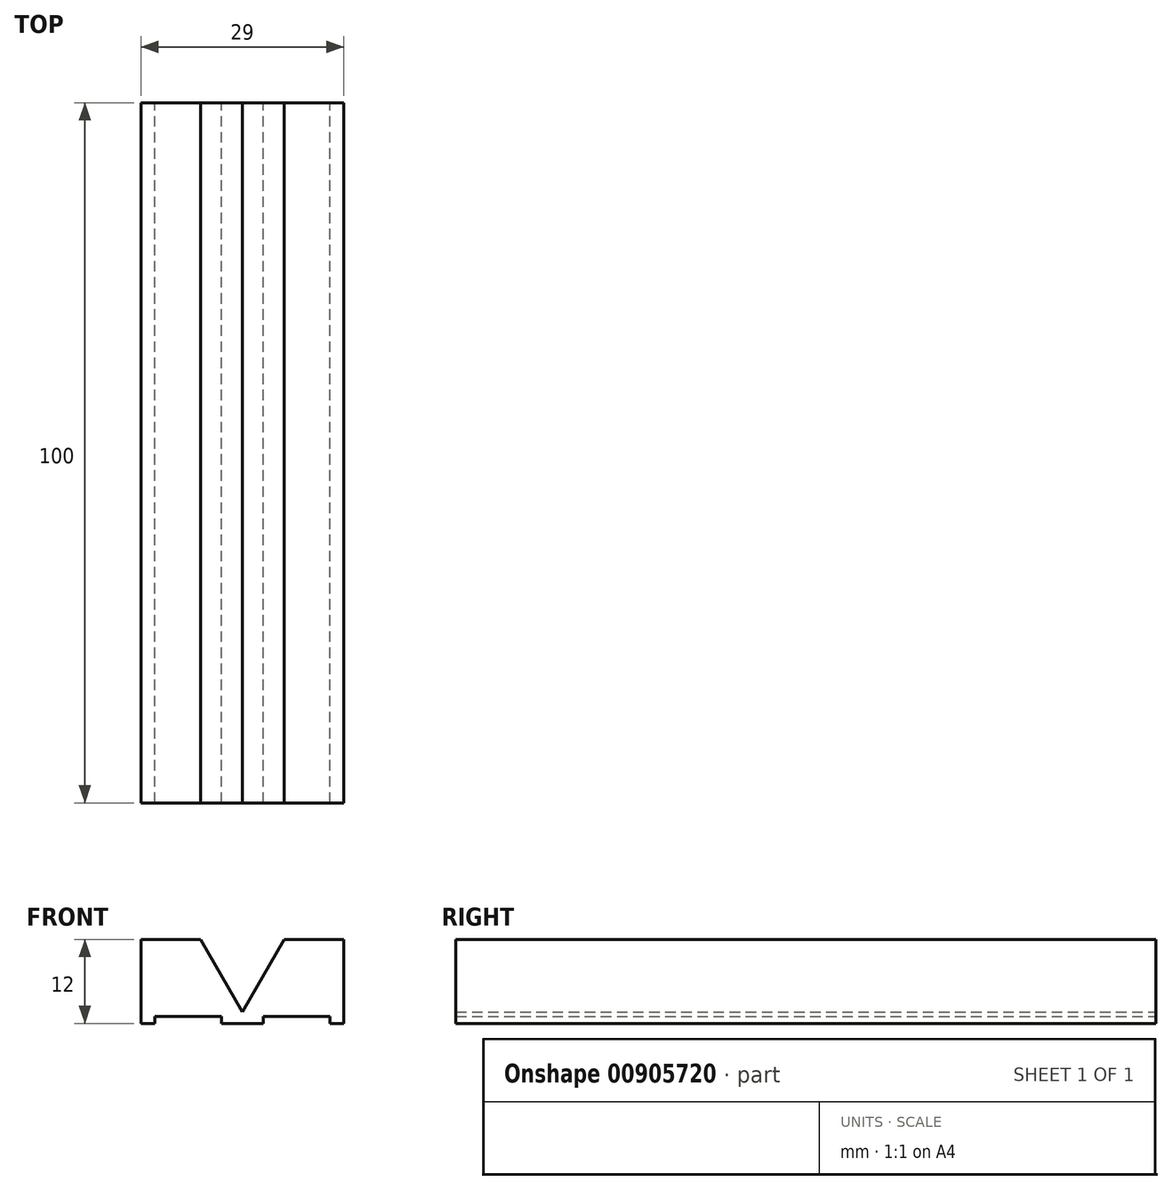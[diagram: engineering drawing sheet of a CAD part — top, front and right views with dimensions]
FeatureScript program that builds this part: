
annotation { "Feature Type Name" : "Feature", "Feature Type Description" : "" }
export const myFeature = defineFeature(function(context is Context, id is Id, definition is map)
    precondition{}
    {
        {
            var Q0;
            Q0=qCreatedBy(makeId("Front.planeOp"),FACE);
            var sketch = newSketch(context, id + "F0", { "sketchPlane" : qUnion([Q0])});
            skLineSegment(sketch, "E0.bottom", {"start": v(-14.5, 6) * mm, "end": v(-6, 6) * mm});
            skLineSegment(sketch, "E0.top", {"start": v(-14.5, -6) * mm, "end": v(-12.5, -6) * mm});
            skLineSegment(sketch, "E0.left", {"start": v(-14.5, 6) * mm, "end": v(-14.5, -6) * mm});
            skLineSegment(sketch, "E0.right", {"start": v(14.5, 6) * mm, "end": v(14.5, -6) * mm});
            skPoint(sketch, "E0.middle", {"position": v(0, 0) * mm});
            skLineSegment(sketch, "E1", {"start": v(-6, 6) * mm, "end": v(0, -4.4) * mm});
            skLineSegment(sketch, "E2", {"start": v(0, -4.4) * mm, "end": v(6, 6) * mm});
            skLineSegment(sketch, "E3.trimOffspring", {"start": v(6, 6) * mm, "end": v(14.5, 6) * mm});
            skLineSegment(sketch, "E4.top", {"start": v(-12.5, -5) * mm, "end": v(-3, -5) * mm});
            skLineSegment(sketch, "E4.left", {"start": v(-12.5, -6) * mm, "end": v(-12.5, -5) * mm});
            skLineSegment(sketch, "E4.right", {"start": v(-3, -6) * mm, "end": v(-3, -5) * mm});
            skLineSegment(sketch, "E5.top", {"start": v(3, -5) * mm, "end": v(12.5, -5) * mm});
            skLineSegment(sketch, "E5.left", {"start": v(3, -6) * mm, "end": v(3, -5) * mm});
            skLineSegment(sketch, "E5.right", {"start": v(12.5, -6) * mm, "end": v(12.5, -5) * mm});
            skLineSegment(sketch, "E6.trimOffspring", {"start": v(-3, -6) * mm, "end": v(3, -6) * mm});
            skLineSegment(sketch, "E7.trimOffspring", {"start": v(12.5, -6) * mm, "end": v(14.5, -6) * mm});
            skSolve(sketch);
        }
        {
            var Q0;
            Q0=makeQuery(id+"F0.imprint","IMPRINT",FACE,{"disambiguationData":[TD([[makeQuery(id+"F0.imprint","IMPRINT",EDGE,{"derivedFrom":sQuery(id+"F0.wireOp",EDGE,"E0.bottom")}),-1.0]])]});
            extrude(context, id + "F1", {"entities" : qUnion([Q0]), "endBound" : BoundingType.SYMMETRIC, "depth" : 100 * mm, "offsetDistance" : 25 * mm});
        }
    });
